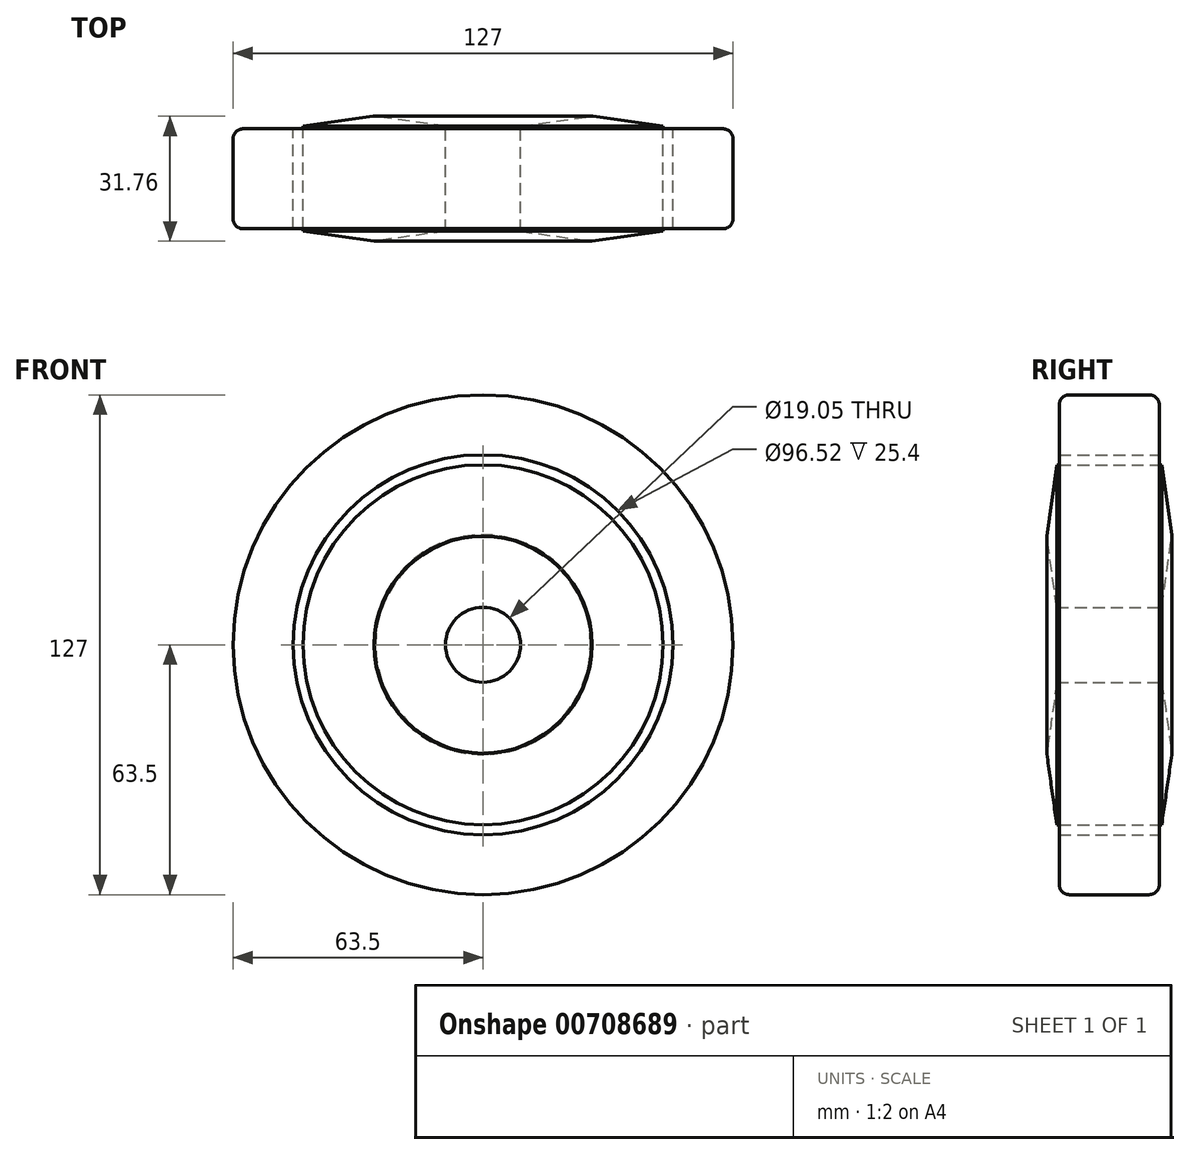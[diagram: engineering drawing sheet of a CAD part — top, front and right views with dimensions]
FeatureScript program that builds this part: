
annotation { "Feature Type Name" : "Feature", "Feature Type Description" : "" }
export const myFeature = defineFeature(function(context is Context, id is Id, definition is map)
    precondition{}
    {
        {
            var Q0;
            Q0=qCreatedBy(makeId("Front.planeOp"),FACE);
            var sketch = newSketch(context, id + "F0", { "sketchPlane" : qUnion([Q0])});
            skCircle(sketch, "E0", {"center": v(0, 0) * mm, "radius": 63.5 * mm});
            skCircle(sketch, "E1", {"center": v(0, 0) * mm, "radius": 48.26 * mm});
            skSolve(sketch);
        }
        {
            var Q0;
            Q0=makeQuery(id+"F0.imprint","IMPRINT",FACE,{"disambiguationData":[TD([[makeQuery(id+"F0.imprint","IMPRINT",EDGE,{"derivedFrom":sQuery(id+"F0.wireOp",EDGE,"E0")}),1.0]])]});
            extrude(context, id + "F1", {"entities" : qUnion([Q0]), "endBound" : BoundingType.SYMMETRIC, "depth" : 25.4 * mm, "offsetDistance" : 25.4 * mm});
        }
        {
            var Q0;
            Q0=makeQuery(id+"F1.opExtrude","SWEPT_FACE",FACE,{"disambiguationData":[OSD([sQuery(id+"F0.wireOp",EDGE,"E0")])]});
            fillet(context, id + "F2", {"entities" : qUnion([Q0]), "radius" : 2.54 * mm, "tangentPropagation" : true, "allowEdgeOverflow" : false});
        }
        {
            var Q0;
            Q0=qCreatedBy(makeId("Front.planeOp"),FACE);
            var sketch = newSketch(context, id + "F3", { "sketchPlane" : qUnion([Q0])});
            skCircle(sketch, "E2", {"center": v(0, 0) * mm, "radius": 45.72 * mm});
            skCircle(sketch, "E3", {"center": v(0, 0) * mm, "radius": 9.53 * mm});
            skSolve(sketch);
        }
        {
            var Q0;
            Q0=makeQuery(id+"F3.imprint","IMPRINT",FACE,{"disambiguationData":[TD([[makeQuery(id+"F3.imprint","IMPRINT",EDGE,{"derivedFrom":sQuery(id+"F3.wireOp",EDGE,"E2")}),1.0]])]});
            extrude(context, id + "F4", {"entities" : qUnion([Q0]), "endBound" : BoundingType.SYMMETRIC, "depth" : 31.75 * mm, "offsetDistance" : 25.4 * mm});
        }
        {
            var Q0;
            Q0=makeQuery(id+"F4.opExtrude","CAP_FACE",FACE,{"disambiguationData":[OSD([sQuery(id+"F3.wireOp",EDGE,"E2"),sQuery(id+"F3.wireOp",EDGE,"E3")])],"isStart":false});
            chamfer(context, id + "F5", {"entities" : qUnion([Q0]), "chamferType" : ChamferType.TWO_OFFSETS, "width1" : 18.03 * mm, "oppositeDirection" : false, "width2" : 2.54 * mm, "tangentPropagation" : true});
        }
        {
            var Q0;
            Q0=makeQuery(id+"F4.opExtrude","CAP_FACE",FACE,{"disambiguationData":[OSD([sQuery(id+"F3.wireOp",EDGE,"E2"),sQuery(id+"F3.wireOp",EDGE,"E3")])],"isStart":true});
            chamfer(context, id + "F6", {"entities" : qUnion([Q0]), "chamferType" : ChamferType.TWO_OFFSETS, "width1" : 2.54 * mm, "oppositeDirection" : false, "width2" : 17.78 * mm, "tangentPropagation" : true});
        }
    });
